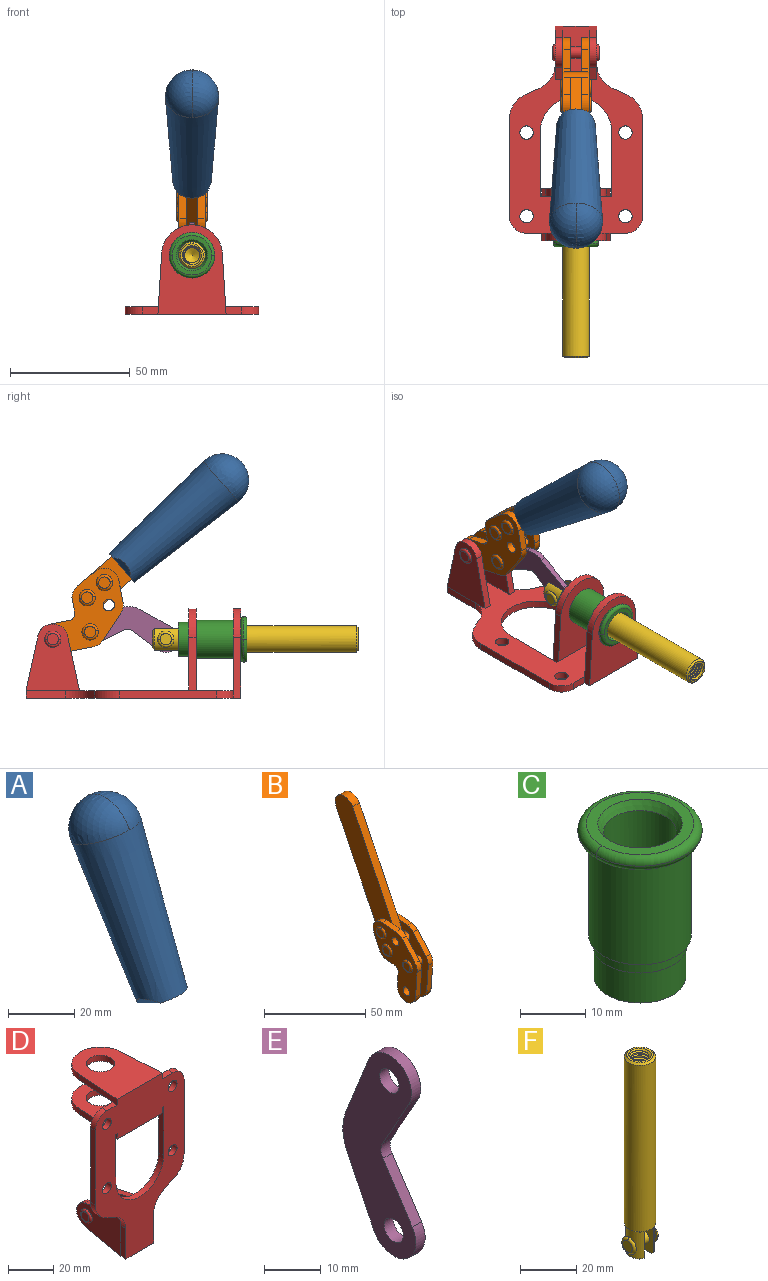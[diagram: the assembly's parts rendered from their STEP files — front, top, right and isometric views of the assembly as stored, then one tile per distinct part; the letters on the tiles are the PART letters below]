
ASSEMBLY  parts=6 mates=5
PART A: 11 faces, bbox 22.3x42.6x64.5 mm
  f0: sphere r=11.13mm, area 411.4mm2, adj f1,f8
  f1: cone r=11.11mm half-angle=3.3deg, axis (0,0.44,0.9), area 3251.8mm2, adj f0,f7,f8,f9,f10
  f2: cylinder r=6.16mm len=11.7mm, axis (1,0,0), area 89.5mm2, adj f3,f4,f5,f6
  f3: plane 60.23x36.75mm, normal (-1,0,0), area 763.6mm2, adj f2,f4,f6,f10
  f4: plane 51.37x25.05mm, normal (0,0.9,-0.44), area 264.2mm2, adj f2,f3,f5,f10
  f5: plane 60.23x36.75mm, normal (1,0,0), area 763.6mm2, adj f2,f4,f6,f10
  f6: plane 51.37x25.05mm, normal (0,-0.9,0.44), area 264.2mm2, adj f2,f3,f5,f10
  f7: plane 9.95x5.95mm, normal (0.71,-0.31,-0.64), area 25.8mm2, adj f1,f10
  f8: sphere r=11.13mm, area 411.4mm2, adj f0,f1
  f9: plane 9.95x5.95mm, normal (-0.71,-0.31,-0.64), area 25.8mm2, adj f1,f10
  f10: plane 14.27x11.38mm, normal (0,-0.44,-0.9), area 106.7mm2, adj f1,f3,f4,f5,f6,f7,f9
PART B: 59 faces, bbox 12.9x60.2x99.6 mm
  f0: torus R=2.39mm, axis (-1,0,0), area 14.9mm2, adj f20,f43,f51
  f1: torus R=2.39mm, axis (-1,0,0), area 14.9mm2, adj f19,f42,f51
  f2: torus R=2.39mm, axis (-1,0,0), area 14.9mm2, adj f18,f35,f51
  f3: torus R=2.39mm, axis (-1,0,0), area 14.9mm2, adj f14,f17,f23
  f4: torus R=2.39mm, axis (-1,0,0), area 14.9mm2, adj f13,f16,f23
  f5: torus R=2.39mm, axis (-1,0,0), area 14.9mm2, adj f12,f15,f23
  f6: cylinder r=2.39mm len=4.78mm, axis (1,0,0), area 46.5mm2, adj f48,f50,f51
  f7: cylinder r=2.39mm len=4.78mm, axis (1,0,0), area 46.5mm2, adj f50,f51
  f8: cylinder r=6.35mm len=12.68mm, axis (1,0,0), area 61.8mm2, adj f38,f39,f50,f51
  f9: cylinder r=2.39mm len=4.78mm, axis (-1,0,0), area 70.5mm2, adj f46,f50
  f10: cylinder r=2.39mm len=4.78mm, axis (-1,0,0), area 46.5mm2, adj f23,f45,f46
  f11: cylinder r=2.39mm len=4.78mm, axis (-1,0,0), area 46.5mm2, adj f23,f46
  f12: plane 4.78x4.78mm, normal (1,0,0), area 17.9mm2, adj f5,f15
  f13: plane 4.78x4.78mm, normal (1,0,0), area 17.9mm2, adj f4,f16
  f14: plane 4.78x4.78mm, normal (1,0,0), area 17.9mm2, adj f3,f17
  f15: torus R=2.39mm, axis (-1,0,0), area 14.9mm2, adj f5,f12,f23
  f16: torus R=2.39mm, axis (-1,0,0), area 14.9mm2, adj f4,f13,f23
  f17: torus R=2.39mm, axis (-1,0,0), area 14.9mm2, adj f3,f14,f23
  f18: plane 4.78x4.78mm, normal (-1,0,0), area 17.9mm2, adj f2,f35
  f19: plane 4.78x4.78mm, normal (-1,0,0), area 17.9mm2, adj f1,f42
  f20: plane 4.78x4.78mm, normal (-1,0,0), area 17.9mm2, adj f0,f43
  f21: plane 2.26x0.2mm, normal (1,0,0), area 0.2mm2, adj f31,f44
  f22: plane 2.26x0.2mm, normal (-1,0,0), area 0.2mm2, adj f41,f44
  f23: plane 39.37x30.77mm, normal (1,0,0), area 565.5mm2, adj f3,f4,f5,f10,f11,f15,f16,f17
  f24: cylinder r=6.1mm len=4.15mm, axis (-1,0,0), area 14.7mm2, adj f23,f25,f32,f46
  f25: plane 10.25x9.01mm, normal (0,-0.75,0.66), area 42.3mm2, adj f23,f24,f26,f46
  f26: cylinder r=6.35mm len=4.64mm, axis (-1,0,0), area 15.6mm2, adj f23,f25,f27,f46
  f27: plane 15.84x3.1mm, normal (0,-1,-0.07), area 49.2mm2, adj f23,f26,f28,f46
  f28: cylinder r=6.35mm len=12.68mm, axis (-1,0,0), area 61.8mm2, adj f23,f27,f29,f46
  f29: plane 8.11x3.1mm, normal (0,1,0.07), area 25.2mm2, adj f23,f28,f30,f46
  f30: cylinder r=3.05mm len=3.25mm, axis (-1,0,0), area 14.8mm2, adj f23,f29,f31,f46
  f31: plane 5.99x3.1mm, normal (0,0.07,-1), area 18.6mm2, adj f21,f23,f30,f44,f46
  f32: plane 9.5x3.1mm, normal (0,-0.07,1), area 29.5mm2, adj f23,f24,f33,f46,f47
  f33: cylinder r=6.1mm len=8.63mm, axis (-1,0,0), area 39.1mm2, adj f23,f32,f34,f47
  f34: plane 8.65x3.96mm, normal (0,0.91,-0.42), area 29.5mm2, adj f23,f33,f44,f47
  f35: torus R=2.39mm, axis (-1,0,0), area 14.9mm2, adj f2,f18,f51
  f36: plane 10.25x9.01mm, normal (0,-0.75,0.66), area 42.3mm2, adj f37,f49,f50,f51
  f37: cylinder r=6.35mm len=4.64mm, axis (1,0,0), area 15.6mm2, adj f36,f38,f50,f51
  f38: plane 15.84x3.1mm, normal (0,-1,-0.07), area 49.2mm2, adj f8,f37,f50,f51
  f39: plane 8.11x3.1mm, normal (0,1,0.07), area 25.2mm2, adj f8,f40,f50,f51
  f40: cylinder r=3.05mm len=3.25mm, axis (1,0,0), area 14.8mm2, adj f39,f41,f50,f51
  f41: plane 5.99x3.1mm, normal (0,0.07,-1), area 18.6mm2, adj f22,f40,f44,f50,f51
  f42: torus R=2.39mm, axis (-1,0,0), area 14.9mm2, adj f1,f19,f51
  f43: torus R=2.39mm, axis (-1,0,0), area 14.9mm2, adj f0,f20,f51
  f44: cylinder r=6.35mm len=12.12mm, axis (-1,0,0), area 128.9mm2, adj f21,f22,f23,f31,f34,f41,f46,f47
  f45: plane 2.65x1.35mm, normal (1,0,0), area 1mm2, adj f10,f55
  f46: plane 39.08x20.42mm, normal (-1,0,0), area 412.5mm2, adj f9,f10,f11,f24,f25,f26,f27,f28
  f47: plane 77.62x39.82mm, normal (1,0,0), area 850mm2, adj f32,f33,f34,f44,f53,f54,f55
  f48: plane 2.65x1.35mm, normal (-1,0,0), area 1mm2, adj f6,f55
  f49: cylinder r=6.1mm len=4.15mm, axis (1,0,0), area 14.7mm2, adj f36,f50,f51,f56
  f50: plane 39.08x20.42mm, normal (1,0,0), area 412.5mm2, adj f6,f7,f8,f9,f36,f37,f38,f39
  f51: plane 39.37x30.77mm, normal (-1,0,0), area 565.5mm2, adj f0,f1,f2,f6,f7,f8,f35,f36
  f52: plane 8.65x3.96mm, normal (0,0.91,-0.42), area 29.5mm2, adj f44,f51,f57,f58
  f53: plane 68.49x33.4mm, normal (0,0.9,-0.44), area 358.1mm2, adj f44,f47,f54,f58
  f54: cylinder r=6.35mm len=12.06mm, axis (1,0,0), area 93.7mm2, adj f47,f53,f55,f58
  f55: plane 68.49x33.4mm, normal (0,-0.9,0.44), area 358.1mm2, adj f44,f45,f46,f47,f48,f50,f54,f58
  f56: plane 9.5x3.1mm, normal (0,-0.07,1), area 29.5mm2, adj f49,f50,f51,f57,f58
  f57: cylinder r=6.1mm len=8.63mm, axis (1,0,0), area 39.1mm2, adj f51,f52,f56,f58
  f58: plane 77.62x39.82mm, normal (-1,0,0), area 850mm2, adj f44,f52,f53,f54,f55,f56,f57
PART C: 15 faces, bbox 20.6x20.6x28.7 mm
  f0: torus R=8.26mm, axis (0,0,1), area 56.8mm2, adj f1,f10,f12
  f1: torus R=8.26mm, axis (0,0,1), area 56.8mm2, adj f0,f6,f13
  f2: cylinder r=5.59mm len=25.91mm, axis (0,0,1), area 909.6mm2, adj f3,f4
  f3: cone r=6.86mm half-angle=45deg, axis (0,0,-1), area 70.2mm2, adj f2,f14
  f4: cone r=6.47mm half-angle=30deg, axis (0,0,1), area 66.7mm2, adj f2,f13
  f5: cylinder r=7.04mm len=14.07mm, axis (0,0,1), area 252.6mm2, adj f11,f14
  f6: torus R=8.26mm, axis (0,0,1), area 56.8mm2, adj f1,f12,f13
  f7: cylinder r=7.16mm len=14.33mm, axis (0,0,1), area 91.5mm2, adj f9,f11
  f8: cylinder r=7.86mm len=18.42mm, axis (0,0,1), area 909.6mm2, adj f9,f10
  f9: plane 15.72x15.72mm, normal (0,0,-1), area 33mm2, adj f7,f8
  f10: plane 16.51x16.51mm, normal (0,0,-1), area 19.9mm2, adj f0,f8,f12
  f11: plane 14.33x14.33mm, normal (0,0,-1), area 5.7mm2, adj f5,f7
  f12: torus R=8.26mm, axis (0,0,1), area 56.8mm2, adj f0,f6,f10
  f13: plane 16.51x16.51mm, normal (0,0,1), area 82.7mm2, adj f1,f4,f6
  f14: plane 14.07x14.07mm, normal (0,0,-1), area 7.8mm2, adj f3,f5
PART D: 55 faces, bbox 55.7x37.4x89.8 mm
  f0: torus R=2.41mm, axis (-1,0,0), area 15mm2, adj f11,f15,f25
  f1: torus R=2.41mm, axis (-1,0,0), area 15mm2, adj f10,f12,f22
  f2: cylinder r=2.78mm len=5.56mm, axis (0,-1,0), area 54.2mm2, adj f30,f54
  f3: cylinder r=14.99mm len=29.97mm, axis (0,-1,0), area 145.9mm2, adj f30,f49,f53,f54
  f4: cylinder r=2.78mm len=5.56mm, axis (0,-1,0), area 54.2mm2, adj f30,f54
  f5: cylinder r=2.78mm len=5.56mm, axis (0,-1,0), area 54.2mm2, adj f30,f54
  f6: cylinder r=2.78mm len=5.56mm, axis (0,-1,0), area 54.2mm2, adj f30,f54
  f7: cylinder r=6.35mm len=12.7mm, axis (0,0,1), area 123.6mm2, adj f27,f51
  f8: cylinder r=6.35mm len=12.7mm, axis (0,0,-1), area 124.7mm2, adj f21,f35
  f9: cylinder r=2.41mm len=11.18mm, axis (-1,0,0), area 169.4mm2, adj f16,f19
  f10: plane 4.83x4.83mm, normal (1,0,0), area 18.3mm2, adj f1,f12
  f11: plane 4.83x4.83mm, normal (-1,0,0), area 18.3mm2, adj f0,f15
  f12: torus R=2.41mm, axis (-1,0,0), area 15mm2, adj f1,f10,f22
  f13: cylinder r=6.35mm len=12.41mm, axis (1,0,0), area 53.4mm2, adj f18,f19,f22,f23
  f14: cylinder r=6.35mm len=12.41mm, axis (-1,0,0), area 53.4mm2, adj f16,f17,f24,f25
  f15: torus R=2.41mm, axis (-1,0,0), area 15mm2, adj f0,f11,f25
  f16: plane 27.86x22.35mm, normal (1,0,0), area 425.4mm2, adj f9,f14,f17,f24,f30
  f17: plane 22.86x4.97mm, normal (0,0.21,0.98), area 72.5mm2, adj f14,f16,f25,f30
  f18: plane 22.86x4.97mm, normal (0,0.21,0.98), area 72.5mm2, adj f13,f19,f22,f30
  f19: plane 27.86x22.35mm, normal (-1,0,0), area 425.4mm2, adj f9,f13,f18,f23,f30
  f20: cylinder r=12.7mm len=25.35mm, axis (0,0,-1), area 119.8mm2, adj f21,f34,f35,f36
  f21: plane 34.21x28.07mm, normal (0,0,-1), area 702.4mm2, adj f8,f20,f30,f34,f36
  f22: plane 27.96x22.45mm, normal (1,0,0), area 407.2mm2, adj f1,f12,f13,f18,f23,f30,f42,f43
  f23: plane 22.86x4.97mm, normal (0,0.21,-0.98), area 72.5mm2, adj f13,f19,f22,f44
  f24: plane 22.86x4.97mm, normal (0,0.21,-0.98), area 72.5mm2, adj f14,f16,f25,f44
  f25: plane 27.86x22.35mm, normal (-1,0,0), area 407.1mm2, adj f0,f14,f15,f17,f24,f30,f45,f46
  f26: plane 3.1x0.95mm, normal (0,0,-1), area 2.7mm2, adj f30,f49,f50,f54
  f27: plane 34.21x28.07mm, normal (0,0,1), area 702.4mm2, adj f7,f28,f30,f50,f52
  f28: cylinder r=12.7mm len=25.35mm, axis (0,0,1), area 118.8mm2, adj f27,f50,f51,f52
  f29: plane 3.1x0.95mm, normal (0,0,-1), area 2.7mm2, adj f30,f52,f53,f54
  f30: plane 86.54x55.63mm, normal (0,1,0), area 2362.9mm2, adj f2,f3,f4,f5,f6,f16,f17,f18
  f31: plane 40.56x3.1mm, normal (-1,0,0), area 125.7mm2, adj f30,f32,f48,f54
  f32: cylinder r=7.11mm len=7.11mm, axis (0,-1,0), area 34.6mm2, adj f30,f31,f33,f54
  f33: plane 6.67x3.1mm, normal (0,0,1), area 20.4mm2, adj f30,f32,f34,f54
  f34: plane 25.39x3.13mm, normal (-1,0.06,0), area 79.5mm2, adj f20,f21,f33,f35,f54
  f35: plane 37.31x28.45mm, normal (0,0,1), area 789.9mm2, adj f8,f20,f34,f36,f54
  f36: plane 25.39x3.13mm, normal (1,0.06,0), area 79.5mm2, adj f20,f21,f35,f37,f54
  f37: plane 6.67x3.1mm, normal (0,0,1), area 20.4mm2, adj f30,f36,f38,f54
  f38: cylinder r=7.11mm len=7.11mm, axis (0,-1,0), area 34.6mm2, adj f30,f37,f39,f54
  f39: plane 40.56x3.1mm, normal (1,0,0), area 125.7mm2, adj f30,f38,f40,f54
  f40: cylinder r=11.18mm len=10.16mm, axis (0,-1,0), area 39.5mm2, adj f30,f39,f41,f54
  f41: plane 6.09x3.1mm, normal (0.42,0,-0.91), area 20.8mm2, adj f30,f40,f42,f54
  f42: cylinder r=11.18mm len=9.41mm, axis (0,-1,0), area 37.2mm2, adj f22,f30,f41,f43,f54
  f43: plane 16.5x3.1mm, normal (1,0,0), area 51.1mm2, adj f22,f42,f44,f54
  f44: plane 17.37x3.1mm, normal (0,0,-1), area 53.8mm2, adj f23,f24,f30,f43,f45,f54
  f45: plane 16.5x3.1mm, normal (-1,0,0), area 51.1mm2, adj f25,f44,f46,f54
  f46: cylinder r=11.18mm len=9.41mm, axis (0,-1,0), area 37.2mm2, adj f25,f30,f45,f47,f54
  f47: plane 6.09x3.1mm, normal (-0.42,0,-0.91), area 20.8mm2, adj f30,f46,f48,f54
  f48: cylinder r=11.18mm len=10.16mm, axis (0,-1,0), area 39.5mm2, adj f30,f31,f47,f54
  f49: plane 26.54x3.1mm, normal (-1,0,0), area 82.3mm2, adj f3,f26,f30,f54
  f50: plane 25.39x3.1mm, normal (1,0.06,0), area 78.8mm2, adj f26,f27,f28,f51,f54
  f51: plane 37.31x28.45mm, normal (0,0,-1), area 789.9mm2, adj f7,f28,f50,f52,f54
  f52: plane 25.39x3.1mm, normal (-1,0.06,0), area 78.8mm2, adj f27,f28,f29,f51,f54
  f53: plane 26.54x3.1mm, normal (1,0,0), area 82.3mm2, adj f3,f29,f30,f54
  f54: plane 89.66x55.63mm, normal (0,-1,0), area 2678.5mm2, adj f2,f3,f4,f5,f6,f26,f29,f31
PART E: 12 faces, bbox 2.3x18.2x42.8 mm
  f0: cylinder r=2.4mm len=4.8mm, axis (1,0,0), area 34.9mm2, adj f4,f11
  f1: cylinder r=10.41mm len=8.47mm, axis (1,0,0), area 20.2mm2, adj f4,f9,f10,f11
  f2: cylinder r=3.05mm len=3.16mm, axis (1,0,0), area 7.7mm2, adj f4,f6,f7,f11
  f3: cylinder r=2.4mm len=4.8mm, axis (1,0,0), area 34.9mm2, adj f4,f11
  f4: plane 42.81x18.23mm, normal (-1,0,0), area 414.1mm2, adj f0,f1,f2,f3,f5,f6,f7,f8
  f5: cylinder r=5.54mm len=10.67mm, axis (1,0,0), area 41.8mm2, adj f4,f6,f10,f11
  f6: plane 11.66x6.53mm, normal (0,-0.87,-0.49), area 30.9mm2, adj f2,f4,f5,f11
  f7: plane 11.17x7.33mm, normal (0,-0.84,0.55), area 30.9mm2, adj f2,f4,f8,f11
  f8: cylinder r=5.54mm len=10.51mm, axis (1,0,0), area 41.8mm2, adj f4,f7,f9,f11
  f9: plane 13.67x6.67mm, normal (0,0.9,-0.44), area 35.1mm2, adj f1,f4,f8,f11
  f10: plane 14.1x5.7mm, normal (0,0.93,0.37), area 35.1mm2, adj f1,f4,f5,f11
  f11: plane 42.81x18.23mm, normal (1,0,0), area 414.1mm2, adj f0,f1,f2,f3,f5,f6,f7,f8
PART F: 48 faces, bbox 12.6x11.1x86.1 mm
  f0: torus R=2.41mm, axis (-1,0,0), area 15mm2, adj f30,f32,f34
  f1: torus R=2.41mm, axis (-1,0,0), area 15mm2, adj f29,f31,f33
  f2: cylinder r=5.54mm len=72.39mm, axis (0,0,1), area 2518.5mm2, adj f3,f4,f42,f43
  f3: cone r=5.54mm half-angle=45deg, axis (0,0,1), area 7.6mm2, adj f2,f5,f41
  f4: cone r=5.54mm half-angle=45deg, axis (0,0,-1), area 34.9mm2, adj f2,f39
  f5: cylinder r=5.08mm len=11.48mm, axis (0,0,1), area 108.3mm2, adj f3,f7,f8,f41
  f6: cylinder r=2.41mm len=4.83mm, axis (-1,0,0), area 71.2mm2, adj f40,f41
  f7: cylinder r=2.41mm len=4.83mm, axis (-1,0,0), area 7.6mm2, adj f5,f34
  f8: cone r=5.08mm half-angle=45deg, axis (0,0,1), area 10.6mm2, adj f5,f37,f41
  f9: cone r=3.98mm half-angle=45deg, axis (0,0,1), area 17.6mm2, adj f27,f39,f45,f46,f47
  f10: cylinder r=2.41mm len=4.83mm, axis (-1,0,0), area 7.6mm2, adj f33,f38
  f11: cylinder r=3.2mm len=6.4mm, axis (0,0,1), area 78.4mm2, adj f12,f28,f44,f45,f47
  f12: cylinder r=3.2mm len=6.4mm, axis (0,0,1), area 10.5mm2, adj f11,f13,f45,f47
  f13: cylinder r=3.2mm len=6.4mm, axis (0,0,1), area 10.5mm2, adj f12,f14,f45,f47
  f14: cylinder r=3.2mm len=6.4mm, axis (0,0,1), area 10.5mm2, adj f13,f15,f45,f47
  f15: cylinder r=3.2mm len=6.4mm, axis (0,0,1), area 10.5mm2, adj f14,f16,f45,f47
  f16: cylinder r=3.2mm len=6.4mm, axis (0,0,1), area 10.5mm2, adj f15,f17,f45,f47
  f17: cylinder r=3.2mm len=6.4mm, axis (0,0,1), area 10.5mm2, adj f16,f18,f45,f47
  f18: cylinder r=3.2mm len=6.4mm, axis (0,0,1), area 10.5mm2, adj f17,f19,f45,f47
  f19: cylinder r=3.2mm len=6.4mm, axis (0,0,1), area 10.5mm2, adj f18,f20,f45,f47
  f20: cylinder r=3.2mm len=6.4mm, axis (0,0,1), area 10.5mm2, adj f19,f21,f45,f47
  f21: cylinder r=3.2mm len=6.4mm, axis (0,0,1), area 10.5mm2, adj f20,f22,f45,f47
  f22: cylinder r=3.2mm len=6.4mm, axis (0,0,1), area 10.5mm2, adj f21,f23,f45,f47
  f23: cylinder r=3.2mm len=6.4mm, axis (0,0,1), area 10.5mm2, adj f22,f24,f45,f47
  f24: cylinder r=3.2mm len=6.4mm, axis (0,0,1), area 10.5mm2, adj f23,f25,f45,f47
  f25: cylinder r=3.2mm len=6.4mm, axis (0,0,1), area 10.5mm2, adj f24,f26,f45,f47
  f26: cylinder r=3.2mm len=6.4mm, axis (0,0,1), area 10.5mm2, adj f25,f27,f45,f47
  f27: cylinder r=3.2mm len=6.4mm, axis (0,0,1), area 7.4mm2, adj f9,f26,f45,f47
  f28: cone r=3.2mm half-angle=60deg, axis (0,0,1), area 37.2mm2, adj f11
  f29: plane 4.83x4.83mm, normal (-1,0,0), area 18.3mm2, adj f1,f31
  f30: plane 4.83x4.83mm, normal (1,0,0), area 18.3mm2, adj f0,f32
  f31: torus R=2.41mm, axis (-1,0,0), area 15mm2, adj f1,f29,f33
  f32: torus R=2.41mm, axis (-1,0,0), area 15mm2, adj f0,f30,f34
  f33: plane 6.83x6.83mm, normal (1,0,0), area 18.3mm2, adj f1,f10,f31
  f34: plane 6.83x6.83mm, normal (-1,0,0), area 18.3mm2, adj f0,f7,f32
  f35: cone r=5.08mm half-angle=45deg, axis (0,0,1), area 10.6mm2, adj f36,f38,f40
  f36: plane 7.25x1.97mm, normal (0,0,-1), area 10mm2, adj f35,f40
  f37: plane 7.25x1.97mm, normal (0,0,-1), area 10mm2, adj f8,f41
  f38: cylinder r=5.08mm len=11.48mm, axis (0,0,1), area 108.3mm2, adj f10,f35,f40,f42
  f39: plane 9.55x9.55mm, normal (0,0,1), area 22mm2, adj f4,f9
  f40: plane 12.76x10.09mm, normal (1,0,0), area 95.7mm2, adj f6,f35,f36,f38,f42,f43
  f41: plane 12.76x10.09mm, normal (-1,0,0), area 95.7mm2, adj f3,f5,f6,f8,f37,f43
  f42: cone r=5.54mm half-angle=45deg, axis (0,0,1), area 7.6mm2, adj f2,f38,f40
  f43: plane 11.07x4.7mm, normal (0,0,-1), area 50.4mm2, adj f2,f40,f41
  f44: plane 0.89x0.62mm, normal (-1,0,0), area 0.3mm2, adj f11,f45,f46,f47
  f45: bspline ~24.8x7.63mm, area 266.6mm2, adj f9,f11,f12,f13,f14,f15,f16,f17
  f46: bspline ~24.87x7.63mm, area 73.6mm2, adj f9,f44,f45,f47
  f47: bspline ~24.98x7.63mm, area 272.5mm2, adj f9,f11,f12,f13,f14,f15,f16,f17
PLACE A rot(axis=(1,0,0),75deg) t=(0,4.15,9.14)mm
PLACE B rot(axis=(1,0,0),75deg) t=(0,4.15,9.14)mm
PLACE C rot(axis=(1,0,0),90deg) t=(0,9.43,0)mm
PLACE D rot(axis=(1,0,0),90deg) t=(0,9.43,0)mm fixed
PLACE E rot(axis=(1,0,0),97.5deg) t=(0,12.88,2.22)mm
PLACE F rot(axis=(1,0,0),90deg) t=(0,9.81,0)mm
MATE revolute B.f7 <-> D.f0  axis (1,0,0) through (0,41.52,24.61)mm
MATE fastened D.f7 <-> C.f0  axis (0,-1,0) through (0,-36.96,24.61)mm
MATE fastened A.f2 <-> B.f54  axis (1,0,0) through (0,-30.37,91.94)mm
MATE revolute B.f4 <-> E.f3  axis (-1,0,0) through (0,25.94,27.64)mm
MATE revolute E.f5 <-> F.f6  axis (1,0,0) through (0,-5.67,24.61)mm
